# Revit family: Shower-Shower_Door-KOHLER-TRILGOY-K-72928T
name_source: partatom
category: Specialty Equipment
revit_build: Autodesk Revit 2017 (Build: 20160225_1515(x64)
units: mm (PartAtom-declared; Revit-internal decimal feet)

## family parameters
Cut with Voids When Loaded = No
Host = Face
OmniClass Number = 23.31.17.17
OmniClass Title = Shower Enclosures
Part Type = Normal
Room Calculation Point = No
Round Connector Dimension = Use Diameter
Shared = No

## types (1)
- SHP-Polished Bright Silver
    ADA Compliant = No
    Assembly Code = C1030200
    Date Modified = 10/14/2020
    Default Elevation = 0"
    Description = TRILGOY HINGE,ANGLE,8MM
    Finish = Kohler-Metal-SHP-Bright_Polished_Silver
    Height = 79 9/16"
    Length = 15 1/16"
    Manufacturer = KOHLER Co.
    Master Format 2014 = 10 28 19.16
    Master Format 2014 Name = Shower Doors
    Material = Premium Metal Construction
    Model = K-72928T-L-SHP
    Product Name = TRILGOY
    Type = 1
    URL = http://www.kohler.com.cn
    WaterSense Certified = No
    Width = 50 1/8"

## geometry (parser evidence)
native form markers: Sweep x6
no freeform markers — native parametric forms only
